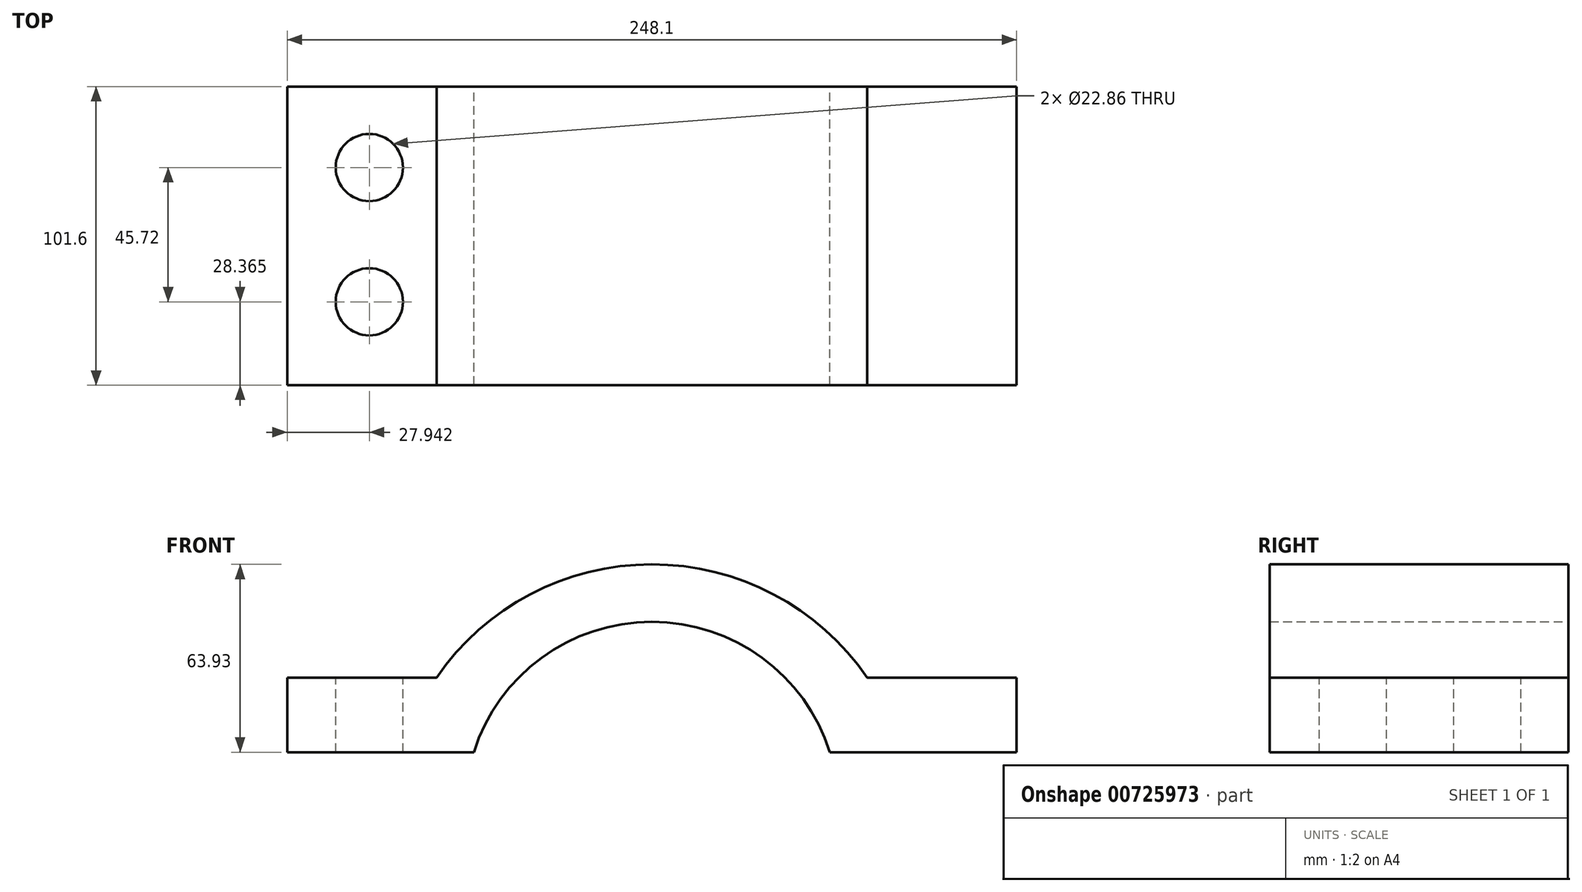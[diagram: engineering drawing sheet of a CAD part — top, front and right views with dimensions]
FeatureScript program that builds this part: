
annotation { "Feature Type Name" : "Feature", "Feature Type Description" : "" }
export const myFeature = defineFeature(function(context is Context, id is Id, definition is map)
    precondition{}
    {
        {
            var Q0;
            Q0=qCreatedBy(makeId("Front.planeOp"),FACE);
            var sketch = newSketch(context, id + "F0", { "sketchPlane" : qUnion([Q0])});
            skLineSegment(sketch, "E0", {"start": v(-132.14, -44.02) * mm, "end": v(-132.14, -18.62) * mm});
            skLineSegment(sketch, "E1", {"start": v(-132.14, -18.62) * mm, "end": v(-81.34, -18.62) * mm});
            skLineSegment(sketch, "E2", {"start": v(115.96, -44.02) * mm, "end": v(115.96, -18.62) * mm});
            skLineSegment(sketch, "E3", {"start": v(115.96, -18.62) * mm, "end": v(65.16, -18.62) * mm});
            skArc(sketch, "E4", {"start": v(65.16, -18.62) * mm, "mid": v(-8.1, 19.9) * mm, "end": v(-81.34, -18.62) * mm});
            skLineSegment(sketch, "E5", {"start": v(-132.14, -44.02) * mm, "end": v(-68.64, -44.02) * mm});
            skLineSegment(sketch, "E6", {"start": v(115.96, -44.02) * mm, "end": v(52.46, -44.02) * mm});
            skArc(sketch, "E7", {"start": v(52.46, -44.02) * mm, "mid": v(-8.1, 0.35) * mm, "end": v(-68.64, -44.02) * mm});
            skSolve(sketch);
        }
        {
            var Q0;
            Q0=makeQuery(id+"F0.imprint","IMPRINT",FACE,{"disambiguationData":[TD([[makeQuery(id+"F0.imprint","IMPRINT",EDGE,{"derivedFrom":sQuery(id+"F0.wireOp",EDGE,"E0")}),-1.0]])]});
            var Q1;
            Q1 = qSketchRegion(id + "F2", true);
            extrude(context, id + "F1", {"entities" : qUnion([Q0, Q1]), "depth" : 101.6 * mm, "offsetDistance" : 25.4 * mm});
        }
        {
            var Q0;
            Q0=makeQuery(id+"F1.opExtrude","SWEPT_FACE",FACE,{"disambiguationData":[OSD([sQuery(id+"F0.wireOp",EDGE,"E1")])]});
            var sketch = newSketch(context, id + "F2", { "sketchPlane" : qUnion([Q0])});
            skCircle(sketch, "E8", {"center": v(-104.2, -27.51) * mm, "radius": 11.43 * mm});
            skCircle(sketch, "E9", {"center": v(-104.2, -73.23) * mm, "radius": 11.43 * mm});
            skArc(sketch, "E10", {"start": v(90.56, -39.37) * mm, "mid": v(79.13, -50.8) * mm, "end": v(90.56, -62.23) * mm});
            skLineSegment(sketch, "E11", {"start": v(90.56, -39.37) * mm, "end": v(115.96, -39.37) * mm});
            skLineSegment(sketch, "E12", {"start": v(90.56, -62.23) * mm, "end": v(115.96, -62.23) * mm});
            skSolve(sketch);
        }
        {
            var Q0;
            Q0=sQuery(id+"F2.wireOp",VERTEX,"E8.center");
            var Q1;
            Q1=sQuery(id+"F2.wireOp",VERTEX,"E9.center");
            var Q2;
            Q2=makeQuery(id+"F1.opExtrude","SWEPT_BODY",BODY,{"disambiguationData":[OSD([sQuery(id+"F0.wireOp",EDGE,"E0"),sQuery(id+"F0.wireOp",EDGE,"E1"),sQuery(id+"F0.wireOp",EDGE,"E2"),sQuery(id+"F0.wireOp",EDGE,"E3"),sQuery(id+"F0.wireOp",EDGE,"E4"),sQuery(id+"F0.wireOp",EDGE,"E5"),sQuery(id+"F0.wireOp",EDGE,"E6"),sQuery(id+"F0.wireOp",EDGE,"E7")])]});
            hole(context, id + "F3", {"style" : HoleStyle.SIMPLE, "endStyle" : HoleEndStyle.THROUGH, "holeDiameter" : 22.86 * mm, "majorDiameter" : 6.35 * mm, "isTappedThrough" : true, "tappedDepth" : 12.7 * mm, "tapClearance" : 3, "locations" : qUnion([Q0, Q1]), "scope" : qUnion([Q2])});
        }
        {
            var Q0;
            Q0=sQuery(id+"F2.wireOp",EDGE,"E10");
            extrude(context, id + "F4", {"bodyType" : ToolBodyType.SURFACE, "surfaceEntities" : qUnion([Q0]), "depth" : 90.17 * mm, "offsetDistance" : 25.4 * mm});
        }
    });
